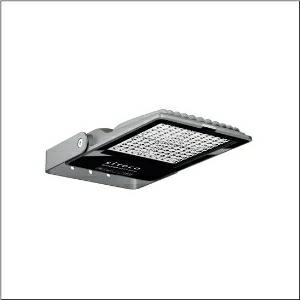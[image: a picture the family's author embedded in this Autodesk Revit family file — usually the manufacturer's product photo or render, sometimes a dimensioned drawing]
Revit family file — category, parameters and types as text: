
# Revit family: sicompact_r__31_mini___pl32_5xa7571b2k23_8fae
name_source: partatom
category: Lighting Fixtures
units: mm (PartAtom-declared; Revit-internal decimal feet)

## family parameters
Cut with Voids When Loaded = No
Host = Face
Light Source = No
Part Type = Normal
Room Calculation Point = No
Round Connector Dimension = Use Diameter
Shared = No

## types (1)
- SiCompact® 31 mini  PL32 (1 x LED, 8000 lm, 47 W, 4000K)
    Apparent Load = 47 VA
    CIE Flux Codes = 32 69 98 100 100
    Color Rendering = 70
    Color Temperature = 4000K
    Default Elevation = 1800 mm
    Description = SiCompact® 31 mini, floodlight, primary light control with lens, of plastic, of toughened safety glass, transparent, light distribution: PL32, light emission: direct distribution, primary light characteristic: asymmetric, installation type: surface-mounted, LED, High Power LED, rated luminous flux: 8.000lm, luminous efficacy: 170lm/W, light colour: 740, colour temperature: 4000K, control gear: ON/OFF, with cable, 3x 1.5mm², mains connection: 220..240V, AC, 50/60Hz, connection cable pre-assembled, cable length: 2m, rated input power: 47W, of diecast aluminium, specular, metallic grey (RAL 9006), length: 461mm, width: 261mm, height: 62mm, bracket, of sheet steel, coated, metallic grey (RAL 9006), ON/OFF, protection rating (complete): IP66, insulation class (complete): insulation class I (protective earthing), certification: CE, ENEC, impact resistance: IK08, permissible operating ambient temperature: -40..+45°C, packaging unit: 1 piece

Light Distribution: PL32
    Height = 62 mm  [stored 0.203412 ft]
    Lamp = 1 x LED
    Lamp Light Flux = 8000 lm
    Lamp Power = 47 W
    Lamp count = 1
    Length = 460 mm
    Luminous efficacy = 170 lm/W
    Manufacturer = Siteco
    ModVariant = No
    Model = 5XA7571B2K23
    Mounting Place = Wall
    Mounting Type = Surface mounted
    Number of Poles = 1
    OnlyDefault = Yes
    Power Factor = 1
    Product Name = SiCompact® 31 mini | PL32
    Product group = floodlight | wall mounted
    ProductGroupID = 2001
    Protection Class = Protection class I
    Protection Degree = IP 66
    RLX_Detail_Level = 1
    RLX_Emergency_Light_Flux = 0 lm
    RLX_Emergency_Type = 0
    RLX_Emergency_Type_DB = No
    RlxData = <blob elided: 126665 chars, md5=d9972b33>
    Socket = socket
    Standby Power = 0 W
    System Light Flux = 8000 lm
    System Power = 47 W
    Type Comments = Product without accessories
    Type Image = l_1006951.jpg
    URL = http://relux.com
    VarID = ---
    Voltage = 0 V
    Weight = 0.00 kg
    Width = 260 mm

note: [stored X ft] marks values corroborated as IEEE doubles in the binary element streams (Revit-internal decimal feet)

## geometry (parser evidence)
native form markers: Blend x4, Sweep x13
no freeform markers — native parametric forms only
